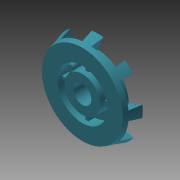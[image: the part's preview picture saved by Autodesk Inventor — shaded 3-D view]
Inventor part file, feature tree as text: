
AUTODESK INVENTOR PART (.ipt)
format: ipt  version: 2014 (Build 180170000, 170)  size: 246,272 bytes
history: native  units: in
note: dims shown in document units (in); Inventor stores cm internally (conversion verified against a paired STEP export)
features: sketch x8, extrude x5, pattern_circular x2, plane x1, loft x1, chamfer x1, revolve x1
ambient origin geometry x8: Origin, YZ Plane, XZ Plane, XY Plane, X Axis, Y Axis, Z Axis, Center Point
bodies: Body1 (feature_tree)
feature tree (19):
  sketch  "Sketch14"  dims[d60=1.73in d61=-0.3275in]
  plane  "Work Plane4"
  loft  "Loft3"
  extrude  "Extrusion9"  TaperAngle=0.0deg  [1 undecoded]
  extrude  "Extrusion10"  Depth=0.385in
  extrude  "Extrusion11"  Depth=1.065in
  pattern_circular  "Circular Pattern3"  Count=4 Angle=360.0deg
  extrude  "Extrusion12"  Depth=0.025in
  chamfer  "Chamfer1"  Distance=0.1495in
  extrude  "Extrusion13"  Depth=0.025in
  revolve  "Revolution2"  [1 undecoded]
  pattern_circular  "Circular Pattern4"  [2 undecoded]
  sketch  "Sketch15"  dims[d62=1.93in d63=0.0in d64=90.0deg]
  sketch  "Sketch16"  dims[d65=0.0in d66=90.0deg d67=0.385in]
  sketch  "Sketch17"  dims[d68=1.0in d69=0.0in d70=1.065in]
  sketch  "Sketch18"  dims[d71=0.76in]
  sketch  "Sketch19"  dims[d72=0.235in d73=0.0in]
  sketch  "Sketch20"  dims[d74=0.0625in]
  sketch  "Sketch21"  dims[d75=0.1375in d76=0.0in d77=1.5748in d78=360.0deg d80=0.124in d85=0.1495in d86=0.0143in d87=0.0143in d88=0.1375in d89=0.0in d90=0.02in d91=0.125in d92=45.0deg d93=22.5deg d94=0.25in d95=0.25in d96=0.25in d97=0.25in d98=0.3in d99=0.23in d100=0.0in d101=0.025in d102=0.025in d103=0.025in d104=0.1in d105=90.0deg d106=3.1496in d107=360.0deg]
note: 4 required parameter values undecoded (feature->parameter linkage not recoverable at this tier; creation-order binding heuristic only, values carry confidence <= 0.55)